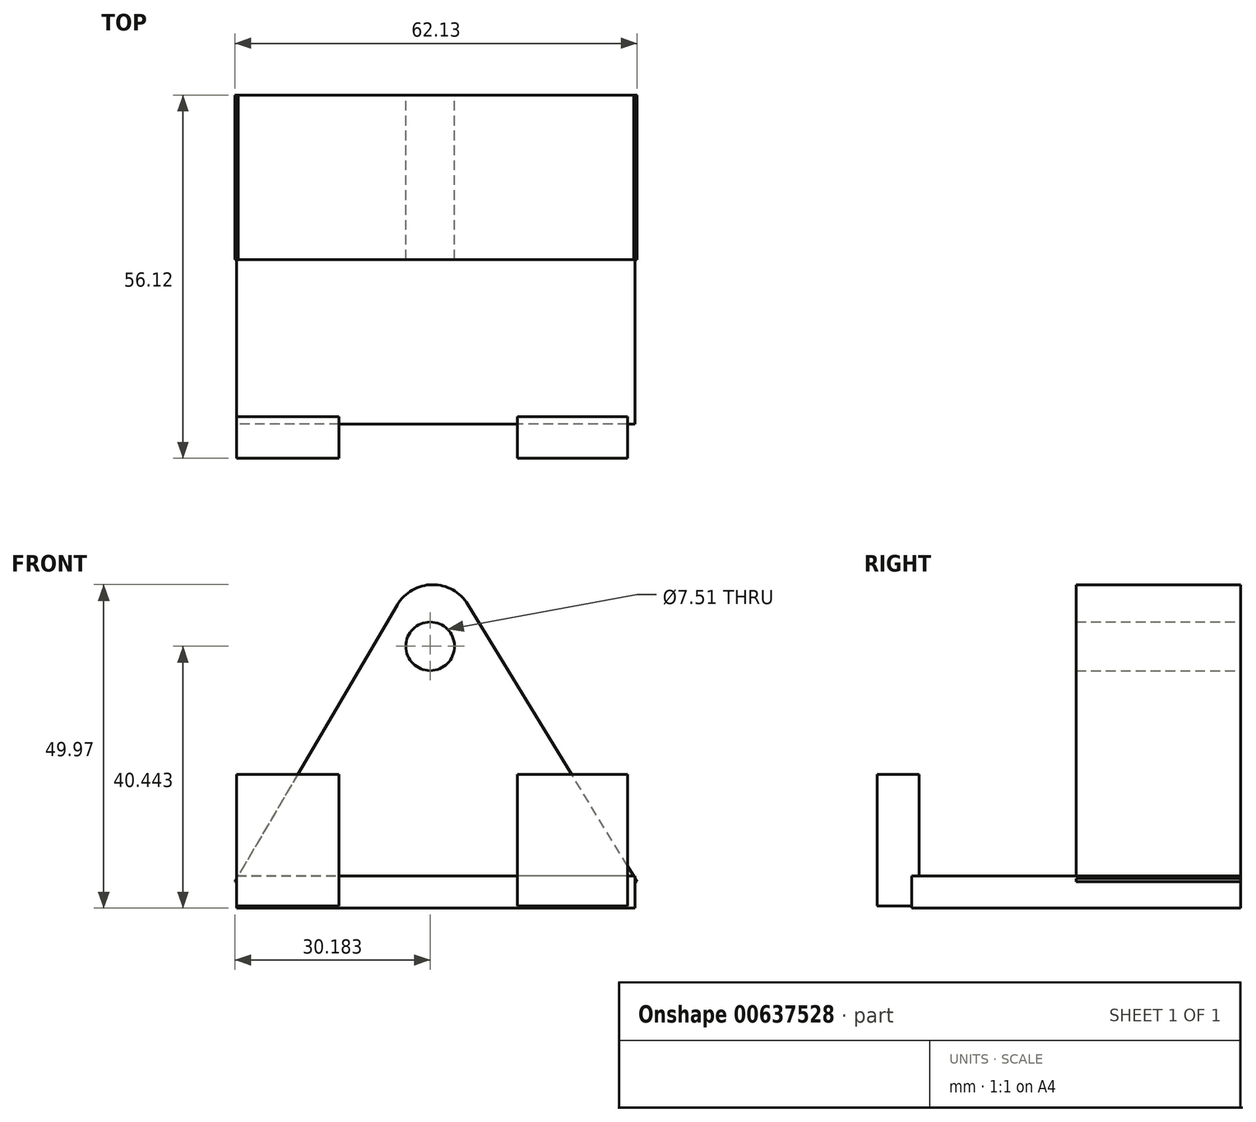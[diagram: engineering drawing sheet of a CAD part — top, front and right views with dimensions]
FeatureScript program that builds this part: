
annotation { "Feature Type Name" : "Feature", "Feature Type Description" : "" }
export const myFeature = defineFeature(function(context is Context, id is Id, definition is map)
    precondition{}
    {
        {
            var Q0;
            Q0=qCreatedBy(makeId("Front.planeOp"),FACE);
            var sketch = newSketch(context, id + "F0", { "sketchPlane" : qUnion([Q0])});
            skLineSegment(sketch, "E0", {"start": v(-33.26, -16.56) * mm, "end": v(28.87, -16.56) * mm});
            skLineSegment(sketch, "E1", {"start": v(28.87, -16.56) * mm, "end": v(2.74, 26.26) * mm});
            skLineSegment(sketch, "E2", {"start": v(-8.16, 26.17) * mm, "end": v(-33.26, -16.56) * mm});
            skPoint(sketch, "E3.visualSharp", {"position": v(-2.78, 35.32) * mm});
            skArc(sketch, "E3.filletArc", {"start": v(2.74, 26.26) * mm, "mid": v(-2.73, 29.3) * mm, "end": v(-8.16, 26.17) * mm});
            skCircle(sketch, "E4", {"center": v(-3.08, 19.78) * mm, "radius": 3.75 * mm});
            skSolve(sketch);
        }
        {
            var Q0;
            Q0 = qSketchRegion(id + "F0", true);
            extrude(context, id + "F1", {"entities" : qUnion([Q0]), "depth" : 25.4 * mm, "offsetDistance" : 25.4 * mm});
        }
        {
            var Q0;
            Q0=qCreatedBy(makeId("Front.planeOp"),FACE);
            var sketch = newSketch(context, id + "F2", { "sketchPlane" : qUnion([Q0])});
            skLineSegment(sketch, "E5.bottom", {"start": v(-32.97, -15.68) * mm, "end": v(28.57, -15.68) * mm});
            skLineSegment(sketch, "E5.top", {"start": v(-32.97, -20.66) * mm, "end": v(28.57, -20.66) * mm});
            skLineSegment(sketch, "E5.left", {"start": v(-32.97, -15.68) * mm, "end": v(-32.97, -20.66) * mm});
            skLineSegment(sketch, "E5.right", {"start": v(28.57, -15.68) * mm, "end": v(28.57, -20.66) * mm});
            skLineSegment(sketch, "E6.bottom", {"start": v(-32.97, -20.66) * mm, "end": v(-18.91, -20.66) * mm});
            skLineSegment(sketch, "E6.left", {"start": v(-32.97, -20.66) * mm, "end": v(-32.97, -15.68) * mm});
            skLineSegment(sketch, "E7.bottom", {"start": v(28.57, -20.66) * mm, "end": v(11.67, -20.66) * mm});
            skLineSegment(sketch, "E7.left", {"start": v(28.57, -20.66) * mm, "end": v(28.57, -15.68) * mm});
            skPoint(sketch, "E8.orphan", {"position": v(11.67, -9.82) * mm});
            skPoint(sketch, "E9.orphan", {"position": v(-18.91, -9.82) * mm});
            skPoint(sketch, "E10.start.orphan", {"position": v(-18.91, -13.26) * mm});
            skPoint(sketch, "E11.start.orphan", {"position": v(11.67, -13.26) * mm});
            skSolve(sketch);
        }
        {
            var Q0;
            Q0 = qSketchRegion(id + "F2", true);
            extrude(context, id + "F3", {"entities" : qUnion([Q0]), "operationType" : NewBodyOperationType.ADD, "depth" : 50.8 * mm, "offsetDistance" : 25.4 * mm});
        }
        {
            var Q0;
            Q0=qCreatedBy(makeId("Top.planeOp"),FACE);
            var sketch = newSketch(context, id + "F4", { "sketchPlane" : qUnion([Q0])});
            skLineSegment(sketch, "E12.bottom", {"start": v(-32.97, -49.68) * mm, "end": v(-17.15, -49.68) * mm});
            skLineSegment(sketch, "E12.top", {"start": v(-32.97, -56.12) * mm, "end": v(-17.15, -56.12) * mm});
            skLineSegment(sketch, "E12.left", {"start": v(-32.97, -49.68) * mm, "end": v(-32.97, -56.12) * mm});
            skLineSegment(sketch, "E12.right", {"start": v(-17.15, -49.68) * mm, "end": v(-17.15, -56.12) * mm});
            skLineSegment(sketch, "E13.bottom", {"start": v(27.4, -49.68) * mm, "end": v(10.4, -49.68) * mm});
            skLineSegment(sketch, "E13.top", {"start": v(27.4, -56.12) * mm, "end": v(10.4, -56.12) * mm});
            skLineSegment(sketch, "E13.left", {"start": v(27.4, -49.68) * mm, "end": v(27.4, -56.12) * mm});
            skLineSegment(sketch, "E13.right", {"start": v(10.4, -49.68) * mm, "end": v(10.4, -56.12) * mm});
            skSolve(sketch);
        }
        {
            var Q0;
            Q0 = qSketchRegion(id + "F4", true);
            extrude(context, id + "F5", {"entities" : qUnion([Q0]), "operationType" : NewBodyOperationType.ADD, "oppositeDirection" : true, "depth" : 20.32 * mm, "offsetDistance" : 25.4 * mm});
        }
    });
